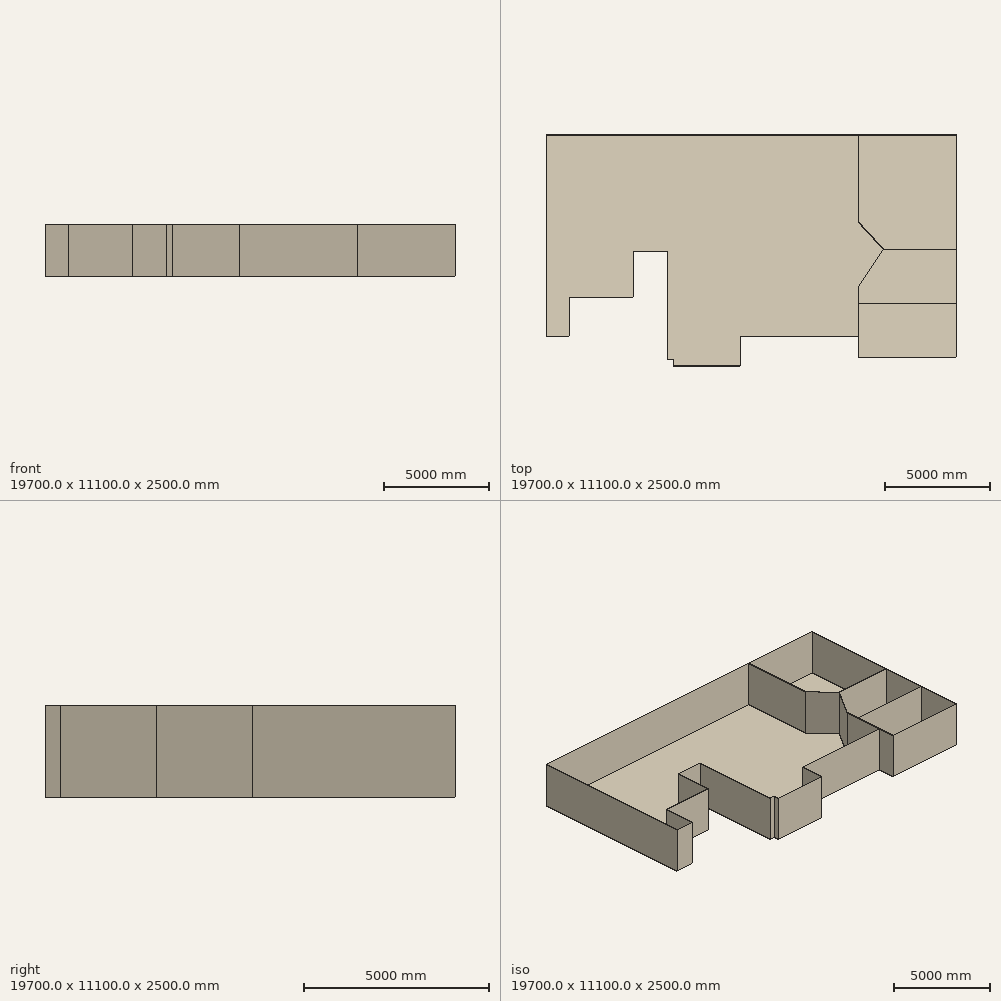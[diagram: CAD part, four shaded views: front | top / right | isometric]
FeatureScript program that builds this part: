
annotation { "Feature Type Name" : "Feature", "Feature Type Description" : "" }
export const myFeature = defineFeature(function(context is Context, id is Id, definition is map)
    precondition{}
    {
        {
            var Q0;
            Q0=qCreatedBy(makeId("Top.planeOp"),FACE);
            var sketch = newSketch(context, id + "F0", { "sketchPlane" : qUnion([Q0])});
            skLineSegment(sketch, "E0.bottom", {"start": v(-19700, 0) * mm, "end": v(0, 0) * mm});
            skLineSegment(sketch, "E0.top", {"start": v(-19700, -9700) * mm, "end": v(-18600, -9700) * mm});
            skLineSegment(sketch, "E0.left", {"start": v(-19700, 0) * mm, "end": v(-19700, -9700) * mm});
            skLineSegment(sketch, "E0.right", {"start": v(0, 0) * mm, "end": v(0, -9700) * mm});
            skLineSegment(sketch, "E1", {"start": v(-4700, 0) * mm, "end": v(-4700, -4200) * mm});
            skLineSegment(sketch, "E2", {"start": v(-4700, -4200) * mm, "end": v(-4110.45, -4838.68) * mm});
            skLineSegment(sketch, "E3", {"start": v(-4700, -9700) * mm, "end": v(-4700, -7296) * mm});
            skLineSegment(sketch, "E4", {"start": v(-4700, -7296) * mm, "end": v(-4000, -6248.33) * mm});
            skLineSegment(sketch, "E5", {"start": v(0, -5500) * mm, "end": v(-3500, -5500) * mm});
            skLineSegment(sketch, "E6", {"start": v(0, -8100) * mm, "end": v(-4700, -8100) * mm});
            skLineSegment(sketch, "E7", {"start": v(-4000, -6248.33) * mm, "end": v(-3500, -5500) * mm});
            skLineSegment(sketch, "E8", {"start": v(-4110.45, -4838.68) * mm, "end": v(-3500, -5500) * mm});
            skLineSegment(sketch, "E9", {"start": v(-10400, -9700) * mm, "end": v(-10400, -11100) * mm});
            skLineSegment(sketch, "E10", {"start": v(-13900, -5600) * mm, "end": v(-13900, -10800) * mm});
            skLineSegment(sketch, "E11", {"start": v(-13900, -5600) * mm, "end": v(-15500, -5600) * mm});
            skLineSegment(sketch, "E12", {"start": v(-15500, -5600) * mm, "end": v(-15500, -7800) * mm});
            skLineSegment(sketch, "E13", {"start": v(-15500, -7800) * mm, "end": v(-18600, -7800) * mm});
            skLineSegment(sketch, "E14", {"start": v(-18600, -7800) * mm, "end": v(-18600, -9700) * mm});
            skLineSegment(sketch, "E15", {"start": v(-13900, -10800) * mm, "end": v(-13600, -10800) * mm});
            skLineSegment(sketch, "E16", {"start": v(-13600, -10800) * mm, "end": v(-13600, -11100) * mm});
            skPoint(sketch, "E17", {"position": v(-13900, -9700) * mm});
            skLineSegment(sketch, "E18.trimOffspring", {"start": v(-10400, -9700) * mm, "end": v(-4700, -9700) * mm});
            skLineSegment(sketch, "E19", {"start": v(-4700, -9700) * mm, "end": v(-4700, -10700) * mm});
            skLineSegment(sketch, "E20", {"start": v(-4700, -10700) * mm, "end": v(0, -10700) * mm});
            skLineSegment(sketch, "E21", {"start": v(0, -10700) * mm, "end": v(0, -9700) * mm});
            skLineSegment(sketch, "E22", {"start": v(-13600, -11100) * mm, "end": v(-10400, -11100) * mm});
            skLineSegment(sketch, "E23", {"start": v(-10400, -10700) * mm, "end": v(-10000, -10007.18) * mm});
            skArc(sketch, "E24", {"start": v(-10000, -10007.18) * mm, "mid": v(-10192.94, -9927.26) * mm, "end": v(-10400, -9900) * mm});
            skPoint(sketch, "E25", {"position": v(-8300, -6900) * mm});
            skPoint(sketch, "E26", {"position": v(-8000, -2800) * mm});
            skPoint(sketch, "E27", {"position": v(-11500, -2800) * mm});
            skPoint(sketch, "E28", {"position": v(-14400, -2800) * mm});
            skSolve(sketch);
        }
        {
            var Q0;
            Q0=makeQuery(id+"F0.imprint","IMPRINT",FACE,{"disambiguationData":[TD([[makeQuery(id+"F0.imprint","IMPRINT",EDGE,{"derivedFrom":sQuery(id+"F0.wireOp",EDGE,"E0.top")}),1.0]])]});
            extrude(context, id + "F1", {"entities" : qUnion([Q0]), "depth" : 2500 * mm, "offsetDistance" : 25 * mm});
        }
        {
            var Q0;
            {var subQ0=sQuery(id+"F0.wireOp",EDGE,"E1");Q0=makeQuery(id+"F0.imprint","IMPRINT",FACE,{"disambiguationData":[TD([[makeQuery(id+"F0.imprint","IMPRINT",EDGE,{"derivedFrom":subQ0}),1.0]])]});}
            extrude(context, id + "F2", {"entities" : qUnion([Q0]), "depth" : 2500 * mm, "offsetDistance" : 25 * mm});
        }
        {
            var Q0;
            {var subQ1=sQuery(id+"F0.wireOp",EDGE,"E4");Q0=makeQuery(id+"F0.imprint","IMPRINT",FACE,{"disambiguationData":[TD([[makeQuery(id+"F0.imprint","IMPRINT",EDGE,{"derivedFrom":subQ1}),-1.0]])]});}
            extrude(context, id + "F3", {"entities" : qUnion([Q0]), "depth" : 2500 * mm, "offsetDistance" : 25 * mm});
        }
        {
            var Q0;
            {var subQ1=sQuery(id+"F0.wireOp",EDGE,"E6");Q0=makeQuery(id+"F0.imprint","IMPRINT",FACE,{"disambiguationData":[TD([[makeQuery(id+"F0.imprint","IMPRINT",EDGE,{"derivedFrom":subQ1}),1.0]])]});}
            extrude(context, id + "F4", {"entities" : qUnion([Q0]), "depth" : 2500 * mm, "offsetDistance" : 25 * mm});
        }
        {
            var Q0;
            Q0=makeQuery(id+"F1.opExtrude","CAP_FACE",FACE,{"disambiguationData":[OSD([sQuery(id+"F0.wireOp",EDGE,"E0.bottom"),sQuery(id+"F0.wireOp",EDGE,"E0.top"),sQuery(id+"F0.wireOp",EDGE,"E0.left"),sQuery(id+"F0.wireOp",EDGE,"E1"),sQuery(id+"F0.wireOp",EDGE,"E2"),sQuery(id+"F0.wireOp",EDGE,"E3"),sQuery(id+"F0.wireOp",EDGE,"E4"),sQuery(id+"F0.wireOp",EDGE,"E7"),sQuery(id+"F0.wireOp",EDGE,"E8"),sQuery(id+"F0.wireOp",EDGE,"E9"),sQuery(id+"F0.wireOp",EDGE,"E10"),sQuery(id+"F0.wireOp",EDGE,"E11"),sQuery(id+"F0.wireOp",EDGE,"E12"),sQuery(id+"F0.wireOp",EDGE,"E13"),sQuery(id+"F0.wireOp",EDGE,"E14"),sQuery(id+"F0.wireOp",EDGE,"E15"),sQuery(id+"F0.wireOp",EDGE,"E16"),sQuery(id+"F0.wireOp",EDGE,"E18.trimOffspring"),sQuery(id+"F0.wireOp",EDGE,"E22")])],"isStart":false});
            var Q1;
            Q1=makeQuery(id+"F2.opExtrude","CAP_FACE",FACE,{"disambiguationData":[OSD([sQuery(id+"F0.wireOp",EDGE,"E0.bottom"),sQuery(id+"F0.wireOp",EDGE,"E0.right"),sQuery(id+"F0.wireOp",EDGE,"E1"),sQuery(id+"F0.wireOp",EDGE,"E2"),sQuery(id+"F0.wireOp",EDGE,"E5"),sQuery(id+"F0.wireOp",EDGE,"E8")])],"isStart":false});
            var Q2;
            Q2=makeQuery(id+"F3.opExtrude","CAP_FACE",FACE,{"disambiguationData":[OSD([sQuery(id+"F0.wireOp",EDGE,"E0.right"),sQuery(id+"F0.wireOp",EDGE,"E3"),sQuery(id+"F0.wireOp",EDGE,"E4"),sQuery(id+"F0.wireOp",EDGE,"E5"),sQuery(id+"F0.wireOp",EDGE,"E6"),sQuery(id+"F0.wireOp",EDGE,"E7")])],"isStart":false});
            var Q3;
            Q3=makeQuery(id+"F4.opExtrude","CAP_FACE",FACE,{"disambiguationData":[OSD([sQuery(id+"F0.wireOp",EDGE,"E0.right"),sQuery(id+"F0.wireOp",EDGE,"E3"),sQuery(id+"F0.wireOp",EDGE,"E6"),sQuery(id+"F0.wireOp",EDGE,"E19"),sQuery(id+"F0.wireOp",EDGE,"E20"),sQuery(id+"F0.wireOp",EDGE,"E21")])],"isStart":false});
            shell(context, id + "F5", {"entities" : qUnion([Q0, Q1, Q2, Q3]), "thickness" : 1 * mm});
        }
    });
